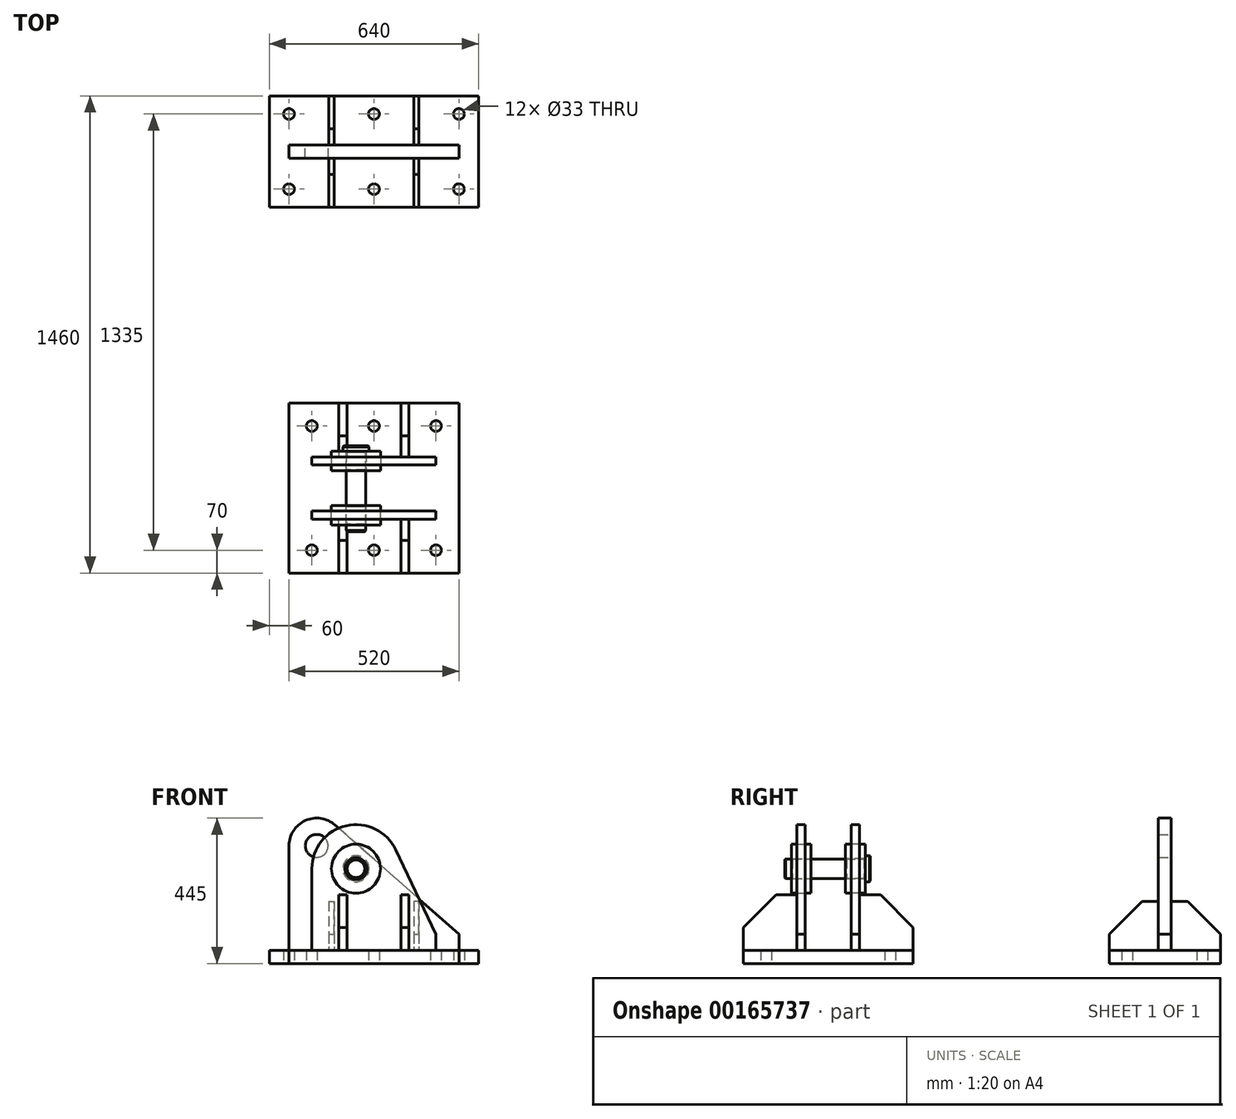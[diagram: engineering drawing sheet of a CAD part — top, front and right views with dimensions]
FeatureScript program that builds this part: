
annotation { "Feature Type Name" : "Feature", "Feature Type Description" : "" }
export const myFeature = defineFeature(function(context is Context, id is Id, definition is map)
    precondition{}
    {
        {
            var Q0;
            Q0=qCreatedBy(makeId("Top.planeOp"),FACE);
            var sketch = newSketch(context, id + "F0", { "sketchPlane" : qUnion([Q0])});
            skLineSegment(sketch, "E0.bottom", {"start": v(-320, 170) * mm, "end": v(320, 170) * mm});
            skLineSegment(sketch, "E0.top", {"start": v(-320, -170) * mm, "end": v(320, -170) * mm});
            skLineSegment(sketch, "E0.left", {"start": v(-320, 170) * mm, "end": v(-320, -170) * mm});
            skLineSegment(sketch, "E0.right", {"start": v(320, 170) * mm, "end": v(320, -170) * mm});
            skLineSegment(sketch, "E1", {"start": v(-320, 170) * mm, "end": v(320, -170) * mm, "construction": true});
            skPoint(sketch, "E2", {"position": v(-260, 115) * mm});
            skLineSegment(sketch, "E3", {"start": v(-320, 0) * mm, "end": v(320, 0) * mm, "construction": true});
            skPoint(sketch, "E4", {"position": v(0, 115) * mm});
            skPoint(sketch, "E5", {"position": v(260, 115) * mm});
            skPoint(sketch, "E6.MirrorP", {"position": v(-260, -115) * mm});
            skPoint(sketch, "E7.MirrorP", {"position": v(0, -115) * mm});
            skPoint(sketch, "E8.MirrorP", {"position": v(260, -115) * mm});
            skSolve(sketch);
        }
        {
            var Q0;
            Q0=makeQuery(id+"F0.imprint","IMPRINT",FACE,{"disambiguationData":[TD([[makeQuery(id+"F0.imprint","IMPRINT",EDGE,{"derivedFrom":sQuery(id+"F0.wireOp",EDGE,"E0.bottom")}),-1.0]])]});
            extrude(context, id + "F1", {"entities" : qUnion([Q0]), "oppositeDirection" : true, "depth" : 40 * mm});
        }
        {
            var Q0;
            Q0=sQuery(id+"F0.wireOp",VERTEX,"E2");
            var Q1;
            Q1=sQuery(id+"F0.wireOp",VERTEX,"E6.MirrorP");
            var Q2;
            Q2=sQuery(id+"F0.wireOp",VERTEX,"E7.MirrorP");
            var Q3;
            Q3=sQuery(id+"F0.wireOp",VERTEX,"E4");
            var Q4;
            Q4=sQuery(id+"F0.wireOp",VERTEX,"E5");
            var Q5;
            Q5=sQuery(id+"F0.wireOp",VERTEX,"E8.MirrorP");
            var Q6;
            Q6=makeQuery(id+"F1.opExtrude","SWEPT_BODY",BODY,{"disambiguationData":[OSD([sQuery(id+"F0.wireOp",EDGE,"E0.bottom"),sQuery(id+"F0.wireOp",EDGE,"E0.top"),sQuery(id+"F0.wireOp",EDGE,"E0.left"),sQuery(id+"F0.wireOp",EDGE,"E0.right")])]});
            hole(context, id + "F2", {"style" : HoleStyle.SIMPLE, "endStyle" : HoleEndStyle.THROUGH, "standardTappedOrClearance" : lookupTablePath({ "standard" : "ISO", "size" : "33", "type" : "Drilled" }), "standardBlindInLast" : lookupTablePath({ "standard" : "ISO", "size" : "33", "type" : "Drilled" }), "holeDiameter" : 33 * mm, "locations" : qUnion([Q0, Q1, Q2, Q3, Q4, Q5]), "scope" : qUnion([Q6]), "isTappedThrough" : true});
        }
        {
            var Q0;
            Q0=qCreatedBy(makeId("Front.planeOp"),FACE);
            var sketch = newSketch(context, id + "F3", { "sketchPlane" : qUnion([Q0])});
            skLineSegment(sketch, "E9", {"start": v(-260, 0) * mm, "end": v(-260, 320) * mm});
            skCircle(sketch, "E10", {"center": v(-175, 320) * mm, "radius": 35 * mm});
            skArc(sketch, "E11", {"start": v(-118.8, 383.78) * mm, "mid": v(-209.99, 397.46) * mm, "end": v(-260, 320) * mm});
            skLineSegment(sketch, "E12", {"start": v(260, 0) * mm, "end": v(260, 50) * mm});
            skLineSegment(sketch, "E13", {"start": v(260, 50) * mm, "end": v(-118.8, 383.78) * mm});
            skLineSegment(sketch, "E14", {"start": v(-260, 0) * mm, "end": v(260, 0) * mm});
            skSolve(sketch);
        }
        {
            var Q0;
            Q0=makeQuery(id+"F3.imprint","IMPRINT",FACE,{"disambiguationData":[TD([[makeQuery(id+"F3.imprint","IMPRINT",EDGE,{"derivedFrom":sQuery(id+"F3.wireOp",EDGE,"E9")}),-1.0]])]});
            extrude(context, id + "F4", {"entities" : qUnion([Q0]), "operationType" : NewBodyOperationType.ADD, "depth" : 40 * mm, "symmetric" : true});
        }
        {
            var Q0;
            Q0=makeQuery(id+"F0.imprint","IMPRINT",FACE,{"disambiguationData":[TD([[makeQuery(id+"F0.imprint","IMPRINT",EDGE,{"derivedFrom":sQuery(id+"F0.wireOp",EDGE,"E0.bottom")}),-1.0]])]});
            var sketch = newSketch(context, id + "F5", { "sketchPlane" : qUnion([Q0])});
            skLineSegment(sketch, "E15.bottom", {"start": v(-138, -20) * mm, "end": v(-122, -20) * mm});
            skLineSegment(sketch, "E15.top", {"start": v(-138, -170) * mm, "end": v(-122, -170) * mm});
            skLineSegment(sketch, "E15.left", {"start": v(-138, -20) * mm, "end": v(-138, -170) * mm});
            skLineSegment(sketch, "E15.right", {"start": v(-122, -20) * mm, "end": v(-122, -170) * mm});
            skLineSegment(sketch, "E16", {"start": v(-260, -115) * mm, "end": v(-138, -115) * mm, "construction": true});
            skLineSegment(sketch, "E17", {"start": v(-122, -115) * mm, "end": v(0, -115) * mm, "construction": true});
            skLineSegment(sketch, "E18.MirrorCS", {"start": v(122, -20) * mm, "end": v(122, -170) * mm});
            skLineSegment(sketch, "E19.MirrorCS", {"start": v(138, -20) * mm, "end": v(138, -170) * mm});
            skLineSegment(sketch, "E20.MirrorCS", {"start": v(-138, 20) * mm, "end": v(-138, 170) * mm});
            skLineSegment(sketch, "E21.MirrorCS", {"start": v(-122, 20) * mm, "end": v(-122, 170) * mm});
            skLineSegment(sketch, "E22.MirrorCS", {"start": v(122, 20) * mm, "end": v(122, 170) * mm});
            skLineSegment(sketch, "E23.MirrorCS", {"start": v(138, 20) * mm, "end": v(138, 170) * mm});
            skLineSegment(sketch, "E24.MirrorCS", {"start": v(138, -20) * mm, "end": v(122, -20) * mm});
            skLineSegment(sketch, "E25.MirrorCS", {"start": v(138, -170) * mm, "end": v(122, -170) * mm});
            skLineSegment(sketch, "E26.MirrorCS", {"start": v(-138, 20) * mm, "end": v(-122, 20) * mm});
            skLineSegment(sketch, "E27.MirrorCS", {"start": v(-138, 170) * mm, "end": v(-122, 170) * mm});
            skLineSegment(sketch, "E28.MirrorCS", {"start": v(138, 20) * mm, "end": v(122, 20) * mm});
            skLineSegment(sketch, "E29.MirrorCS", {"start": v(138, 170) * mm, "end": v(122, 170) * mm});
            skSolve(sketch);
        }
        {
            var Q0;
            Q0=makeQuery(id+"F5.imprint","IMPRINT",FACE,{"disambiguationData":[TD([[makeQuery(id+"F5.imprint","IMPRINT",EDGE,{"derivedFrom":sQuery(id+"F5.wireOp",EDGE,"E15.bottom")}),-1.0]])]});
            var Q1;
            Q1=makeQuery(id+"F5.imprint","IMPRINT",FACE,{"disambiguationData":[TD([[makeQuery(id+"F5.imprint","IMPRINT",EDGE,{"derivedFrom":sQuery(id+"F5.wireOp",EDGE,"E18.MirrorCS")}),1.0]])]});
            var Q2;
            Q2=makeQuery(id+"F5.imprint","IMPRINT",FACE,{"disambiguationData":[TD([[makeQuery(id+"F5.imprint","IMPRINT",EDGE,{"derivedFrom":sQuery(id+"F5.wireOp",EDGE,"E22.MirrorCS")}),-1.0]])]});
            var Q3;
            Q3=makeQuery(id+"F5.imprint","IMPRINT",FACE,{"disambiguationData":[TD([[makeQuery(id+"F5.imprint","IMPRINT",EDGE,{"derivedFrom":sQuery(id+"F5.wireOp",EDGE,"E20.MirrorCS")}),-1.0]])]});
            extrude(context, id + "F6", {"entities" : qUnion([Q0, Q1, Q2, Q3]), "operationType" : NewBodyOperationType.ADD, "depth" : 150 * mm});
        }
        {
            var Q0;
            Q0=makeQuery(id+"F6.opExtrude","CAP_EDGE",EDGE,{"disambiguationData":[OSD([sQuery(id+"F5.wireOp",EDGE,"E15.top")])],"isStart":false});
            var Q1;
            Q1=makeQuery(id+"F6.opExtrude","CAP_EDGE",EDGE,{"disambiguationData":[OSD([sQuery(id+"F5.wireOp",EDGE,"E25.MirrorCS")])],"isStart":false});
            var Q2;
            Q2=makeQuery(id+"F6.opExtrude","CAP_EDGE",EDGE,{"disambiguationData":[OSD([sQuery(id+"F5.wireOp",EDGE,"E29.MirrorCS")])],"isStart":false});
            var Q3;
            Q3=makeQuery(id+"F6.opExtrude","CAP_EDGE",EDGE,{"disambiguationData":[OSD([sQuery(id+"F5.wireOp",EDGE,"E27.MirrorCS")])],"isStart":false});
            chamfer(context, id + "F7", {"entities" : qUnion([Q0, Q1, Q2, Q3]), "width" : 100 * mm, "tangentPropagation" : true});
        }
        {
            var Q0;
            Q0=qCreatedBy(makeId("Top.planeOp"),FACE);
            var sketch = newSketch(context, id + "F8", { "sketchPlane" : qUnion([Q0])});
            skLineSegment(sketch, "E30.bottom", {"start": v(-260, -770) * mm, "end": v(260, -770) * mm});
            skLineSegment(sketch, "E30.top", {"start": v(-260, -1290) * mm, "end": v(260, -1290) * mm});
            skLineSegment(sketch, "E30.left", {"start": v(-260, -770) * mm, "end": v(-260, -1290) * mm});
            skLineSegment(sketch, "E30.right", {"start": v(260, -770) * mm, "end": v(260, -1290) * mm});
            skLineSegment(sketch, "E31", {"start": v(-260, -770) * mm, "end": v(260, -1290) * mm, "construction": true});
            skPoint(sketch, "E32", {"position": v(0, -1030) * mm});
            skPoint(sketch, "E33", {"position": v(-190, -840) * mm});
            skPoint(sketch, "E34", {"position": v(0, -840) * mm});
            skPoint(sketch, "E35", {"position": v(190, -840) * mm});
            skPoint(sketch, "E36", {"position": v(-190, -1220) * mm});
            skPoint(sketch, "E37", {"position": v(0, -1220) * mm});
            skPoint(sketch, "E38", {"position": v(190, -1220) * mm});
            skLineSegment(sketch, "E39", {"start": v(0, -770) * mm, "end": v(0, -1290) * mm, "construction": true});
            skLineSegment(sketch, "E40", {"start": v(-260, -1030) * mm, "end": v(260, -1030) * mm, "construction": true});
            skSolve(sketch);
        }
        {
            var Q0;
            Q0=makeQuery(id+"F8.imprint","IMPRINT",FACE,{"disambiguationData":[TD([[makeQuery(id+"F8.imprint","IMPRINT",EDGE,{"derivedFrom":sQuery(id+"F8.wireOp",EDGE,"E30.bottom")}),-1.0]])]});
            extrude(context, id + "F9", {"entities" : qUnion([Q0]), "oppositeDirection" : true, "depth" : 40 * mm});
        }
        {
            var Q0;
            Q0=sQuery(id+"F8.wireOp",VERTEX,"E33");
            var Q1;
            Q1=sQuery(id+"F8.wireOp",VERTEX,"E34");
            var Q2;
            Q2=sQuery(id+"F8.wireOp",VERTEX,"E35");
            var Q3;
            Q3=sQuery(id+"F8.wireOp",VERTEX,"E36");
            var Q4;
            Q4=sQuery(id+"F8.wireOp",VERTEX,"E37");
            var Q5;
            Q5=sQuery(id+"F8.wireOp",VERTEX,"E38");
            var Q6;
            Q6=makeQuery(id+"F9.opExtrude","SWEPT_BODY",BODY,{"disambiguationData":[OSD([sQuery(id+"F8.wireOp",EDGE,"E30.bottom"),sQuery(id+"F8.wireOp",EDGE,"E30.top"),sQuery(id+"F8.wireOp",EDGE,"E30.left"),sQuery(id+"F8.wireOp",EDGE,"E30.right")])]});
            hole(context, id + "F10", {"style" : HoleStyle.SIMPLE, "endStyle" : HoleEndStyle.THROUGH, "standardTappedOrClearance" : lookupTablePath({ "standard" : "ISO", "size" : "33", "type" : "Drilled" }), "standardBlindInLast" : lookupTablePath({ "standard" : "ISO", "size" : "33", "type" : "Drilled" }), "holeDiameter" : 33 * mm, "locations" : qUnion([Q0, Q1, Q2, Q3, Q4, Q5]), "scope" : qUnion([Q6]), "isTappedThrough" : true});
        }
        {
            var Q0;
            Q0=sQuery(id+"F8.wireOp",EDGE,"E40");
            cPlane(context, id + "F11", {"entities" : qUnion([Q0]), "cplaneType" : CPlaneType.LINE_ANGLE, "offset" : 25 * mm, "angle" : 0 * degree, "width" : 150 * mm, "height" : 150 * mm});
        }
        {
            var Q0;
            Q0=qCreatedBy(id+"F11.planeOp",FACE);
            cPlane(context, id + "F12", {"entities" : qUnion([Q0]), "cplaneType" : CPlaneType.OFFSET, "offset" : 83 * mm, "width" : 150 * mm, "height" : 150 * mm});
        }
        {
            var Q0;
            Q0=qCreatedBy(id+"F12.planeOp",FACE);
            var sketch = newSketch(context, id + "F13", { "sketchPlane" : qUnion([Q0])});
            skLineSegment(sketch, "E41", {"start": v(190, 0) * mm, "end": v(190, 250) * mm});
            skLineSegment(sketch, "E42", {"start": v(-190, 0) * mm, "end": v(-190, 50) * mm});
            skArc(sketch, "E43", {"start": v(190, 250) * mm, "mid": v(84.8, 381.67) * mm, "end": v(-66.84, 308.13) * mm});
            skLineSegment(sketch, "E44", {"start": v(-190, 50) * mm, "end": v(-66.84, 308.13) * mm});
            skLineSegment(sketch, "E45", {"start": v(190, 0) * mm, "end": v(-190, 0) * mm});
            skCircle(sketch, "E46", {"center": v(55, 250) * mm, "radius": 75 * mm});
            skCircle(sketch, "E47", {"center": v(55, 250) * mm, "radius": 30.5 * mm});
            skSolve(sketch);
        }
        {
            var Q0;
            Q0=makeQuery(id+"F13.imprint","IMPRINT",FACE,{"disambiguationData":[TD([[makeQuery(id+"F13.imprint","IMPRINT",EDGE,{"derivedFrom":sQuery(id+"F13.wireOp",EDGE,"E41")}),1.0]])]});
            extrude(context, id + "F14", {"entities" : qUnion([Q0]), "depth" : 25 * mm, "symmetric" : true});
        }
        {
            var Q0;
            Q0=makeQuery(id+"F13.imprint","IMPRINT",FACE,{"disambiguationData":[TD([[makeQuery(id+"F13.imprint","IMPRINT",EDGE,{"derivedFrom":sQuery(id+"F13.wireOp",EDGE,"E46")}),1.0]])]});
            extrude(context, id + "F15", {"entities" : qUnion([Q0]), "depth" : 60 * mm, "hasSecondDirection" : true, "secondDirectionOppositeDirection" : true, "secondDirectionDepth" : 30 * mm, "symmetric" : true});
        }
        {
            var Q0;
            Q0=makeQuery(id+"F15.opExtrude","CAP_EDGE",EDGE,{"disambiguationData":[OSD([sQuery(id+"F13.wireOp",EDGE,"E47")])],"isStart":false});
            var Q1;
            Q1=makeQuery(id+"F15.opExtrude","CAP_EDGE",EDGE,{"disambiguationData":[OSD([sQuery(id+"F13.wireOp",EDGE,"E47")])],"isStart":true});
            chamfer(context, id + "F16", {"entities" : qUnion([Q0, Q1]), "width" : 3 * mm, "tangentPropagation" : true});
        }
        {
            var Q0;
            Q0=makeQuery(id+"F8.imprint","IMPRINT",FACE,{"disambiguationData":[TD([[makeQuery(id+"F8.imprint","IMPRINT",EDGE,{"derivedFrom":sQuery(id+"F8.wireOp",EDGE,"E30.bottom")}),-1.0]])]});
            var sketch = newSketch(context, id + "F17", { "sketchPlane" : qUnion([Q0])});
            skLineSegment(sketch, "E48.bottom", {"start": v(-107.5, -770) * mm, "end": v(-82.5, -770) * mm});
            skLineSegment(sketch, "E48.top", {"start": v(-107.5, -934.5) * mm, "end": v(-82.5, -934.5) * mm});
            skLineSegment(sketch, "E48.left", {"start": v(-107.5, -770) * mm, "end": v(-107.5, -934.5) * mm});
            skLineSegment(sketch, "E48.right", {"start": v(-82.5, -770) * mm, "end": v(-82.5, -934.5) * mm});
            skLineSegment(sketch, "E49.bottom", {"start": v(82.5, -770) * mm, "end": v(107.5, -770) * mm});
            skLineSegment(sketch, "E49.top", {"start": v(82.5, -934.5) * mm, "end": v(107.5, -934.5) * mm});
            skLineSegment(sketch, "E49.left", {"start": v(82.5, -770) * mm, "end": v(82.5, -934.5) * mm});
            skLineSegment(sketch, "E49.right", {"start": v(107.5, -770) * mm, "end": v(107.5, -934.5) * mm});
            skLineSegment(sketch, "E50", {"start": v(-190, -840) * mm, "end": v(-107.5, -840) * mm, "construction": true});
            skLineSegment(sketch, "E51", {"start": v(-82.5, -840) * mm, "end": v(0, -840) * mm, "construction": true});
            skLineSegment(sketch, "E52", {"start": v(0, -840) * mm, "end": v(82.5, -840) * mm, "construction": true});
            skSolve(sketch);
        }
        {
            var Q0;
            Q0=makeQuery(id+"F17.imprint","IMPRINT",FACE,{"disambiguationData":[TD([[makeQuery(id+"F17.imprint","IMPRINT",EDGE,{"derivedFrom":sQuery(id+"F17.wireOp",EDGE,"E48.bottom")}),-1.0]])]});
            var Q1;
            Q1=makeQuery(id+"F17.imprint","IMPRINT",FACE,{"disambiguationData":[TD([[makeQuery(id+"F17.imprint","IMPRINT",EDGE,{"derivedFrom":sQuery(id+"F17.wireOp",EDGE,"E49.bottom")}),-1.0]])]});
            extrude(context, id + "F18", {"entities" : qUnion([Q0, Q1]), "depth" : 170 * mm});
        }
        {
            var Q0;
            Q0=makeQuery(id+"F18.opExtrude","CAP_EDGE",EDGE,{"disambiguationData":[OSD([sQuery(id+"F17.wireOp",EDGE,"E48.bottom")])],"isStart":false});
            var Q1;
            Q1=makeQuery(id+"F18.opExtrude","CAP_EDGE",EDGE,{"disambiguationData":[OSD([sQuery(id+"F17.wireOp",EDGE,"E49.bottom")])],"isStart":false});
            chamfer(context, id + "F19", {"entities" : qUnion([Q0, Q1]), "width" : 100 * mm, "tangentPropagation" : true});
        }
        {
            var Q0;
            Q0=makeQuery(id+"F14.opExtrude","SWEPT_BODY",BODY,{"disambiguationData":[OSD([sQuery(id+"F13.wireOp",EDGE,"E41"),sQuery(id+"F13.wireOp",EDGE,"E42"),sQuery(id+"F13.wireOp",EDGE,"E43"),sQuery(id+"F13.wireOp",EDGE,"E44"),sQuery(id+"F13.wireOp",EDGE,"E45"),sQuery(id+"F13.wireOp",EDGE,"E46")])]});
            var Q1;
            Q1=makeQuery(id+"F15.opExtrude","SWEPT_BODY",BODY,{"disambiguationData":[OSD([sQuery(id+"F13.wireOp",EDGE,"E46"),sQuery(id+"F13.wireOp",EDGE,"E47")])]});
            var Q2;
            Q2=makeQuery(id+"F18.opExtrude","SWEPT_BODY",BODY,{"disambiguationData":[OSD([sQuery(id+"F17.wireOp",EDGE,"E48.bottom"),sQuery(id+"F17.wireOp",EDGE,"E48.top"),sQuery(id+"F17.wireOp",EDGE,"E48.left"),sQuery(id+"F17.wireOp",EDGE,"E48.right")])]});
            var Q3;
            Q3=makeQuery(id+"F18.opExtrude","SWEPT_BODY",BODY,{"disambiguationData":[OSD([sQuery(id+"F17.wireOp",EDGE,"E49.bottom"),sQuery(id+"F17.wireOp",EDGE,"E49.top"),sQuery(id+"F17.wireOp",EDGE,"E49.left"),sQuery(id+"F17.wireOp",EDGE,"E49.right")])]});
            var Q4;
            Q4=qCreatedBy(id+"F11.planeOp",FACE);
            mirror(context, id + "F20", {"entities" : qUnion([Q0, Q1, Q2, Q3]), "mirrorPlane" : qUnion([Q4])});
        }
        {
            var Q0;
            Q0=makeQuery(id+"F15.opExtrude","CAP_FACE",FACE,{"disambiguationData":[OSD([sQuery(id+"F13.wireOp",EDGE,"E46"),sQuery(id+"F13.wireOp",EDGE,"E47")])],"isStart":false});
            var sketch = newSketch(context, id + "F21", { "sketchPlane" : qUnion([Q0])});
            skCircle(sketch, "E53", {"center": v(55, 250) * mm, "radius": 30 * mm});
            skCircle(sketch, "E54", {"center": v(55, 250) * mm, "radius": 40 * mm});
            skSolve(sketch);
        }
        {
            var Q0;
            Q0=makeQuery(id+"F21.imprint","IMPRINT",FACE,{"disambiguationData":[TD([[makeQuery(id+"F21.imprint","IMPRINT",EDGE,{"derivedFrom":sQuery(id+"F21.wireOp",EDGE,"E53")}),1.0]])]});
            extrude(context, id + "F22", {"entities" : qUnion([Q0]), "oppositeDirection" : true, "depth" : (2 * (83 + 30) + 20) * mm});
        }
        {
            var Q0;
            Q0=makeQuery(id+"F22.opExtrude","CAP_FACE",FACE,{"disambiguationData":[OSD([sQuery(id+"F21.wireOp",EDGE,"E53")])],"isStart":true});
            var Q1;
            Q1=makeQuery(id+"F21.imprint","IMPRINT",FACE,{"disambiguationData":[TD([[makeQuery(id+"F21.imprint","IMPRINT",EDGE,{"derivedFrom":sQuery(id+"F21.wireOp",EDGE,"E53")}),-1.0]])]});
            var Q2;
            Q2=makeQuery(id+"F21.imprint","IMPRINT",FACE,{"disambiguationData":[TD([[makeQuery(id+"F21.imprint","IMPRINT",EDGE,{"derivedFrom":sQuery(id+"F21.wireOp",EDGE,"E54")}),1.0]])]});
            extrude(context, id + "F23", {"entities" : qUnion([Q0, Q1, Q2]), "operationType" : NewBodyOperationType.ADD, "depth" : 16 * mm});
        }
        {
            var Q0;
            Q0=makeQuery(id+"F23.opExtrude","CAP_EDGE",EDGE,{"disambiguationData":[OSD([sQuery(id+"F21.wireOp",EDGE,"E54")])],"isStart":false});
            var Q1;
            Q1=makeQuery(id+"F23.opExtrude","CAP_EDGE",EDGE,{"disambiguationData":[OSD([sQuery(id+"F21.wireOp",EDGE,"E54")])],"isStart":true});
            var Q2;
            Q2=makeQuery(id+"F22.opExtrude","CAP_EDGE",EDGE,{"disambiguationData":[OSD([sQuery(id+"F21.wireOp",EDGE,"E53")])],"isStart":false});
            chamfer(context, id + "F24", {"entities" : qUnion([Q0, Q1, Q2]), "width" : 3 * mm, "tangentPropagation" : true});
        }
    });
